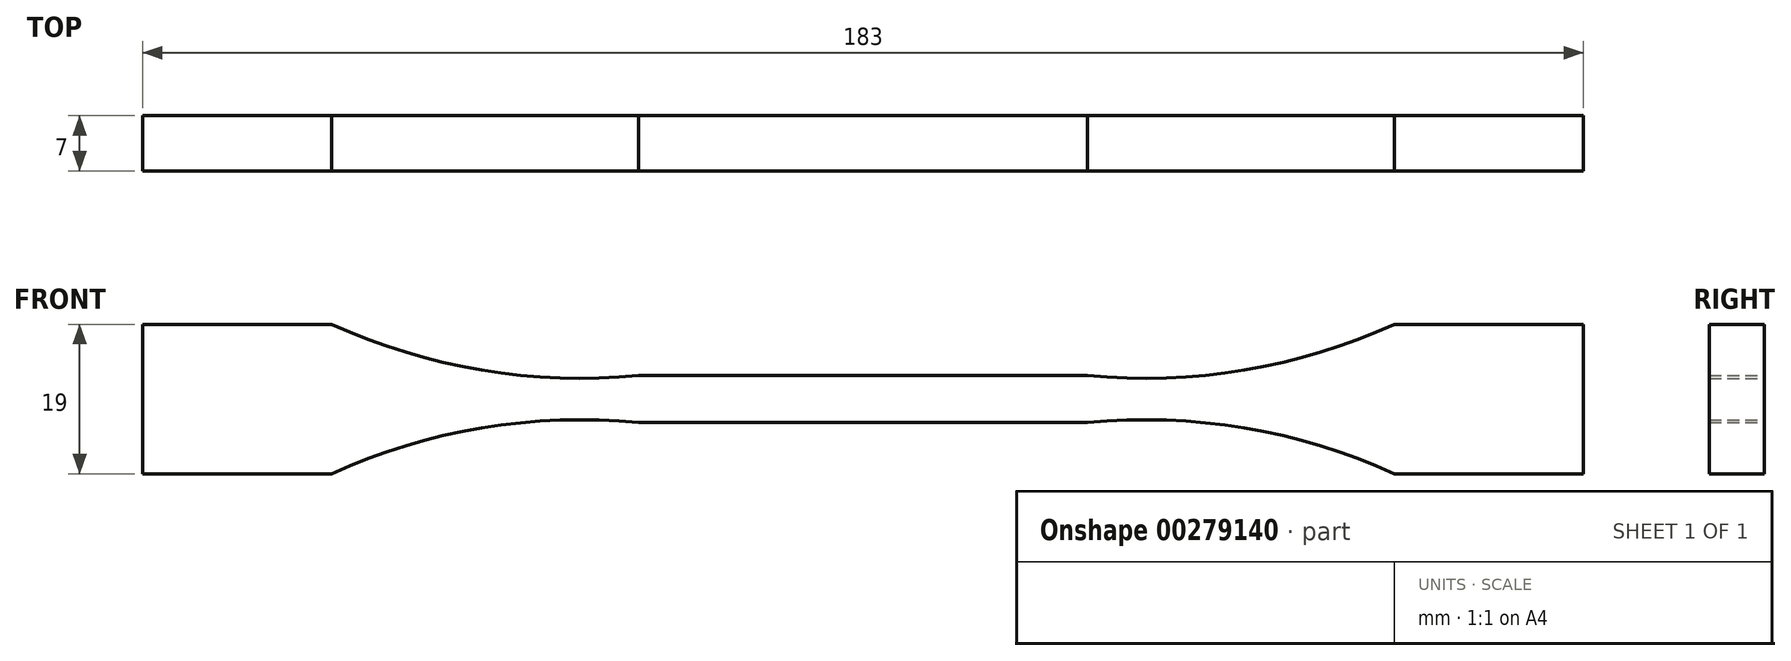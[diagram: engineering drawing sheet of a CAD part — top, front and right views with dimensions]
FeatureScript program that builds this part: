
annotation { "Feature Type Name" : "Feature", "Feature Type Description" : "" }
export const myFeature = defineFeature(function(context is Context, id is Id, definition is map)
    precondition{}
    {
        {
            var Q0;
            Q0=qCreatedBy(makeId("Front.planeOp"),FACE);
            var sketch = newSketch(context, id + "F0", { "sketchPlane" : qUnion([Q0])});
            skLineSegment(sketch, "E0", {"start": v(0, 3) * mm, "end": v(28.5, 3) * mm});
            skArc(sketch, "E1", {"start": v(28.5, 3) * mm, "mid": v(48.43, 3.67) * mm, "end": v(67.5, 9.5) * mm});
            skLineSegment(sketch, "E2", {"start": v(67.5, 9.5) * mm, "end": v(91.5, 9.5) * mm});
            skLineSegment(sketch, "E3.MirrorCS", {"start": v(67.5, -9.5) * mm, "end": v(91.5, -9.5) * mm});
            skLineSegment(sketch, "E4.MirrorCS", {"start": v(0, -3) * mm, "end": v(28.5, -3) * mm});
            skArc(sketch, "E5.MirrorCS", {"start": v(28.5, -3) * mm, "mid": v(48.43, -3.67) * mm, "end": v(67.5, -9.5) * mm});
            skArc(sketch, "E6.MirrorCS", {"start": v(-28.5, -3) * mm, "mid": v(-48.43, -3.67) * mm, "end": v(-67.5, -9.5) * mm});
            skLineSegment(sketch, "E7.MirrorCS", {"start": v(0, 3) * mm, "end": v(-28.5, 3) * mm});
            skArc(sketch, "E8.MirrorCS", {"start": v(-28.5, 3) * mm, "mid": v(-48.43, 3.67) * mm, "end": v(-67.5, 9.5) * mm});
            skLineSegment(sketch, "E9.MirrorCS", {"start": v(-67.5, 9.5) * mm, "end": v(-91.5, 9.5) * mm});
            skLineSegment(sketch, "E10.MirrorCS", {"start": v(-67.5, -9.5) * mm, "end": v(-91.5, -9.5) * mm});
            skLineSegment(sketch, "E11.MirrorCS", {"start": v(0, -3) * mm, "end": v(-28.5, -3) * mm});
            skLineSegment(sketch, "E12", {"start": v(91.5, 9.5) * mm, "end": v(91.5, -9.5) * mm});
            skLineSegment(sketch, "E13", {"start": v(-91.5, 9.5) * mm, "end": v(-91.5, -9.5) * mm});
            skSolve(sketch);
        }
        {
            var Q0;
            Q0=makeQuery(id+"F0.imprint","IMPRINT",FACE,{"disambiguationData":[TD([[makeQuery(id+"F0.imprint","IMPRINT",EDGE,{"derivedFrom":sQuery(id+"F0.wireOp",EDGE,"E0")}),-1.0]])]});
            extrude(context, id + "F1", {"entities" : qUnion([Q0]), "endBound" : BoundingType.SYMMETRIC, "depth" : 7 * mm});
        }
    });
